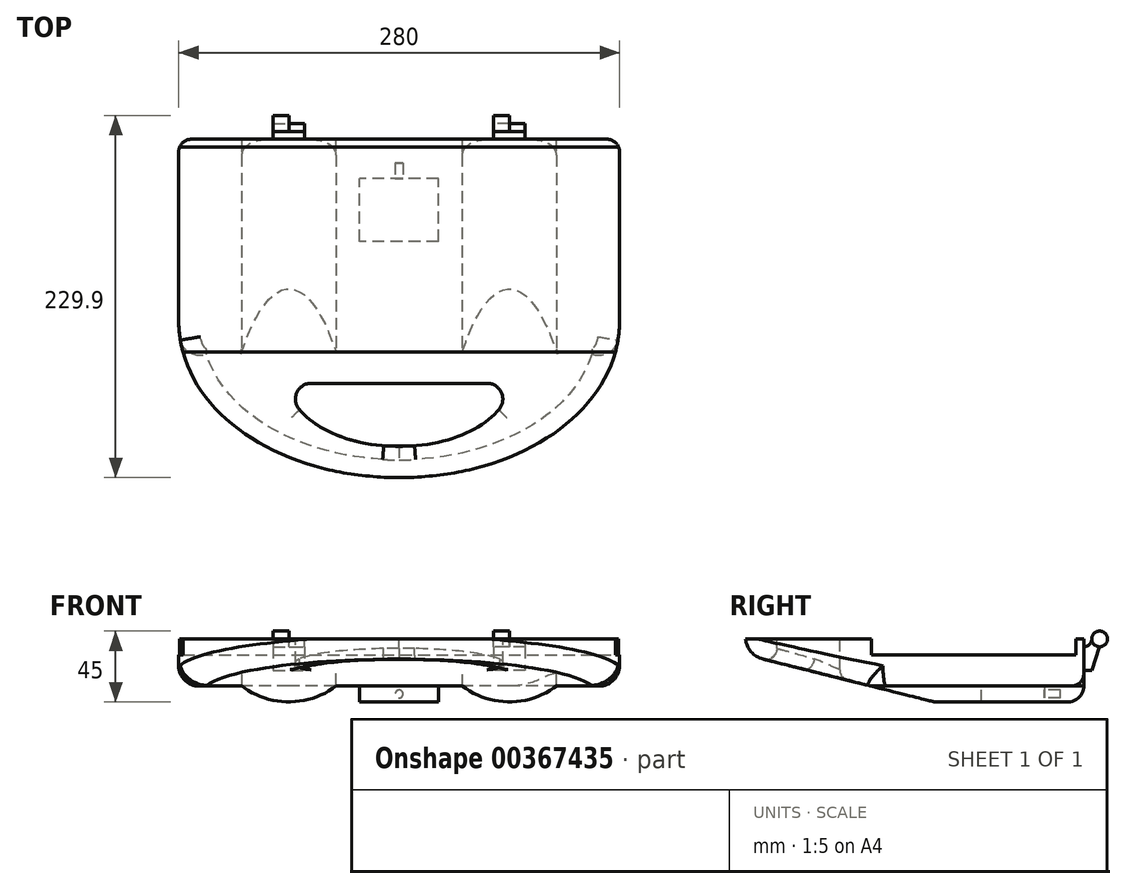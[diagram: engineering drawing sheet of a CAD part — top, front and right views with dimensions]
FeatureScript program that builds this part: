
annotation { "Feature Type Name" : "Feature", "Feature Type Description" : "" }
export const myFeature = defineFeature(function(context is Context, id is Id, definition is map)
    precondition{}
    {
        {
            var Q0;
            Q0=qCreatedBy(makeId("Front.planeOp"),FACE);
            var sketch = newSketch(context, id + "F0", { "sketchPlane" : qUnion([Q0])});
            skLineSegment(sketch, "E0", {"start": v(0, 0) * mm, "end": v(-140, 0) * mm});
            skLineSegment(sketch, "E1", {"start": v(-140, 0) * mm, "end": v(-140, -40) * mm});
            skLineSegment(sketch, "E2", {"start": v(-140, -40) * mm, "end": v(0, -40) * mm});
            skLineSegment(sketch, "E3.MirrorCS", {"start": v(140, -40) * mm, "end": v(0, -40) * mm});
            skLineSegment(sketch, "E4.MirrorCS", {"start": v(0, 0) * mm, "end": v(140, 0) * mm});
            skLineSegment(sketch, "E5.MirrorCS", {"start": v(140, 0) * mm, "end": v(140, -40) * mm});
            skSolve(sketch);
        }
        {
            var Q0;
            Q0=makeQuery(id+"F0.imprint","IMPRINT",FACE,{"disambiguationData":[TD([[makeQuery(id+"F0.imprint","IMPRINT",EDGE,{"derivedFrom":sQuery(id+"F0.wireOp",EDGE,"E0")}),1.0]])]});
            extrude(context, id + "F1", {"entities" : qUnion([Q0]), "endBound" : BoundingType.SYMMETRIC, "depth" : 240 * mm});
        }
        {
            var Q0;
            Q0=makeQuery(id+"F1.opExtrude","SWEPT_FACE",FACE,{"disambiguationData":[OSD([sQuery(id+"F0.wireOp",EDGE,"E5.MirrorCS")])]});
            var sketch = newSketch(context, id + "F2", { "sketchPlane" : qUnion([Q0])});
            skLineSegment(sketch, "E6", {"start": v(-120, 0) * mm, "end": v(-120, -10) * mm});
            skLineSegment(sketch, "E7", {"start": v(-120, -10) * mm, "end": v(-40, -30) * mm});
            skLineSegment(sketch, "E8", {"start": v(-40, -30) * mm, "end": v(0, -40) * mm});
            skLineSegment(sketch, "E9", {"start": v(0, -40) * mm, "end": v(0, -60.45) * mm});
            skLineSegment(sketch, "E10", {"start": v(0, -60.45) * mm, "end": v(-153.05, -60.45) * mm});
            skLineSegment(sketch, "E11", {"start": v(-153.05, -60.45) * mm, "end": v(-153.05, 0) * mm});
            skLineSegment(sketch, "E12", {"start": v(-153.05, 0) * mm, "end": v(-120, 0) * mm});
            skSolve(sketch);
        }
        {
            var Q0;
            Q0=makeQuery(id+"F1.opExtrude","SWEPT_FACE",FACE,{"disambiguationData":[OSD([sQuery(id+"F0.wireOp",EDGE,"E0"),sQuery(id+"F0.wireOp",EDGE,"E4.MirrorCS")])]});
            var sketch = newSketch(context, id + "F3", { "sketchPlane" : qUnion([Q0])});
            skFitSpline(sketch, "E13", {"points": [v(0, -120) * mm, v(-140, -20) * mm], "startDerivative": vector(-228.5, 0) * mm, "endDerivative": vector(0, 173.14) * mm});
            skFitSpline(sketch, "E14.MirrorCS", {"points": [v(0, -120) * mm, v(140, -20) * mm], "startDerivative": vector(228.5, 0) * mm, "endDerivative": vector(0, 173.14) * mm});
            skLineSegment(sketch, "E15", {"start": v(-140, -20) * mm, "end": v(-187.85, -20) * mm});
            skLineSegment(sketch, "E16", {"start": v(-187.85, -20) * mm, "end": v(-187.85, -152.6) * mm});
            skLineSegment(sketch, "E17", {"start": v(-187.85, -152.6) * mm, "end": v(0, -152.6) * mm});
            skLineSegment(sketch, "E18.MirrorCS", {"start": v(187.85, -152.6) * mm, "end": v(0, -152.6) * mm});
            skLineSegment(sketch, "E19.MirrorCS", {"start": v(140, -20) * mm, "end": v(187.85, -20) * mm});
            skLineSegment(sketch, "E20.MirrorCS", {"start": v(187.85, -20) * mm, "end": v(187.85, -152.6) * mm});
            skSolve(sketch);
        }
        {
            var Q0;
            Q0=makeQuery(id+"F1.opExtrude","CAP_FACE",FACE,{"disambiguationData":[OSD([sQuery(id+"F0.wireOp",EDGE,"E0"),sQuery(id+"F0.wireOp",EDGE,"E1"),sQuery(id+"F0.wireOp",EDGE,"E2"),sQuery(id+"F0.wireOp",EDGE,"E3.MirrorCS"),sQuery(id+"F0.wireOp",EDGE,"E4.MirrorCS"),sQuery(id+"F0.wireOp",EDGE,"E5.MirrorCS")])],"isStart":false});
            var sketch = newSketch(context, id + "F4", { "sketchPlane" : qUnion([Q0])});
            skLineSegment(sketch, "E21", {"start": v(-140, -30) * mm, "end": v(-100, -30) * mm});
            skArc(sketch, "E22", {"start": v(-100, -30) * mm, "mid": v(-70, -40) * mm, "end": v(-40, -30) * mm});
            skLineSegment(sketch, "E23", {"start": v(-140, -30) * mm, "end": v(-177.9, -30) * mm});
            skLineSegment(sketch, "E24", {"start": v(-177.9, -30) * mm, "end": v(-177.9, -89.34) * mm});
            skLineSegment(sketch, "E25", {"start": v(-177.9, -89.34) * mm, "end": v(0, -89.34) * mm});
            skPoint(sketch, "E26.endSnap0", {"position": v(0, -40) * mm});
            skLineSegment(sketch, "E27", {"start": v(0, -30) * mm, "end": v(-40, -30) * mm});
            skLineSegment(sketch, "E28.MirrorCS", {"start": v(140, -30) * mm, "end": v(100, -30) * mm});
            skArc(sketch, "E29.MirrorCS", {"start": v(100, -30) * mm, "mid": v(70, -40) * mm, "end": v(40, -30) * mm});
            skLineSegment(sketch, "E30.MirrorCS", {"start": v(140, -30) * mm, "end": v(177.9, -30) * mm});
            skLineSegment(sketch, "E31.MirrorCS", {"start": v(177.9, -30) * mm, "end": v(177.9, -89.34) * mm});
            skLineSegment(sketch, "E32.MirrorCS", {"start": v(177.9, -89.34) * mm, "end": v(0, -89.34) * mm});
            skLineSegment(sketch, "E33.MirrorCS", {"start": v(0, -30) * mm, "end": v(40, -30) * mm});
            skSolve(sketch);
        }
        {
            var Q0;
            {var subQ4=sQuery(id+"F3.wireOp",EDGE,"E13");Q0=makeQuery(id+"F3.imprint","IMPRINT",FACE,{"disambiguationData":[TD([[makeQuery(id+"F3.imprint","IMPRINT",EDGE,{"derivedFrom":subQ4}),-1.0]])]});}
            var sketch = newSketch(context, id + "F5", { "sketchPlane" : qUnion([Q0])});
            skFitSpline(sketch, "E34", {"points": [v(0, -100) * mm, v(-70, -60) * mm], "startDerivative": vector(-116.82, -1.18) * mm, "endDerivative": vector(-0.75, 63.41) * mm});
            skLineSegment(sketch, "E35", {"start": v(-55.84, -60) * mm, "end": v(0, -60) * mm});
            skLineSegment(sketch, "E36.MirrorCS", {"start": v(55.84, -60) * mm, "end": v(0, -60) * mm});
            skFitSpline(sketch, "E37.MirrorCS", {"points": [v(0, -100) * mm, v(70, -60) * mm], "startDerivative": vector(116.82, -1.18) * mm, "endDerivative": vector(0.75, 63.41) * mm});
            skArc(sketch, "E38.filletArc", {"start": v(-55.84, -60) * mm, "mid": v(-64.84, -65.66) * mm, "end": v(-63.66, -76.23) * mm});
            skArc(sketch, "E39.filletArc", {"start": v(63.66, -76.23) * mm, "mid": v(64.84, -65.66) * mm, "end": v(55.84, -60) * mm});
            skSolve(sketch);
        }
        {
            var Q0;
            Q0=qSketchRegion(id+"F3",true);
            extrude(context, id + "F6", {"entities" : qUnion([Q0]), "operationType" : NewBodyOperationType.REMOVE, "oppositeDirection" : true, "depth" : 100 * mm});
        }
        {
            var Q0;
            Q0=qSketchRegion(id+"F4",true);
            extrude(context, id + "F7", {"entities" : qUnion([Q0]), "operationType" : NewBodyOperationType.REMOVE, "oppositeDirection" : true, "depth" : 400 * mm});
        }
        {
            var Q0;
            Q0=qSketchRegion(id+"F2",true);
            extrude(context, id + "F8", {"entities" : qUnion([Q0]), "operationType" : NewBodyOperationType.REMOVE, "oppositeDirection" : true, "depth" : 300 * mm});
        }
        {
            var Q0;
            Q0=qSketchRegion(id+"F5",true);
            extrude(context, id + "F9", {"entities" : qUnion([Q0]), "operationType" : NewBodyOperationType.REMOVE, "oppositeDirection" : true, "depth" : 25 * mm});
        }
        {
            var Q0;
            Q0=makeQuery(id+"F1.opExtrude","SWEPT_FACE",FACE,{"disambiguationData":[OSD([sQuery(id+"F0.wireOp",EDGE,"E5.MirrorCS")])]});
            var sketch = newSketch(context, id + "F10", { "sketchPlane" : qUnion([Q0])});
            skLineSegment(sketch, "E40", {"start": v(-40, 0) * mm, "end": v(-40, -10) * mm});
            skLineSegment(sketch, "E41", {"start": v(-40, -10) * mm, "end": v(90, -10) * mm});
            skLineSegment(sketch, "E42", {"start": v(90, -10) * mm, "end": v(90, 19.27) * mm});
            skLineSegment(sketch, "E43", {"start": v(90, 19.27) * mm, "end": v(-40, 19.27) * mm});
            skLineSegment(sketch, "E44", {"start": v(-40, 19.27) * mm, "end": v(-40, 0) * mm});
            skSolve(sketch);
        }
        {
            var Q0;
            Q0=qSketchRegion(id+"F10",true);
            extrude(context, id + "F11", {"entities" : qUnion([Q0]), "operationType" : NewBodyOperationType.REMOVE, "oppositeDirection" : true, "depth" : 300 * mm});
        }
        {
            var Q0;
            Q0=makeQuery(id+"F1.opExtrude","SWEPT_FACE",FACE,{"disambiguationData":[OSD([sQuery(id+"F0.wireOp",EDGE,"E5.MirrorCS")])]});
            var sketch = newSketch(context, id + "F12", { "sketchPlane" : qUnion([Q0])});
            skLineSegment(sketch, "E45", {"start": v(95, 0) * mm, "end": v(95, -52.5) * mm});
            skLineSegment(sketch, "E46", {"start": v(95, -52.5) * mm, "end": v(129.76, -52.5) * mm});
            skLineSegment(sketch, "E47", {"start": v(129.76, -52.5) * mm, "end": v(129.76, 18.92) * mm});
            skLineSegment(sketch, "E48", {"start": v(129.76, 18.92) * mm, "end": v(95, 18.92) * mm});
            skLineSegment(sketch, "E49", {"start": v(95, 18.92) * mm, "end": v(95, 0) * mm});
            skSolve(sketch);
        }
        {
            var Q0;
            Q0=qSketchRegion(id+"F12",true);
            extrude(context, id + "F13", {"entities" : qUnion([Q0]), "operationType" : NewBodyOperationType.REMOVE, "oppositeDirection" : true, "depth" : 300 * mm});
        }
        {
            var Q0;
            Q0=makeQuery(id+"F13.boolean.opBoolean","COPY",FACE,{"derivedFrom":makeQuery(id+"F13.opExtrude","SWEPT_FACE",FACE,{"disambiguationData":[OSD([sQuery(id+"F12.wireOp",EDGE,"E45"),sQuery(id+"F12.wireOp",EDGE,"E49")])]})});
            var sketch = newSketch(context, id + "F14", { "sketchPlane" : qUnion([Q0])});
            skLineSegment(sketch, "E50", {"start": v(-70, -40) * mm, "end": v(-70, 0) * mm});
            skLineSegment(sketch, "E51", {"start": v(-70, -20) * mm, "end": v(-140, -20) * mm});
            skLineSegment(sketch, "E52", {"start": v(70, -40) * mm, "end": v(70, 0) * mm});
            skLineSegment(sketch, "E53", {"start": v(70, -20) * mm, "end": v(140, -20) * mm});
            skSolve(sketch);
        }
        {
            var Q0;
            Q0=sQuery(id+"F14.wireOp",EDGE,"E51");
            var Q1;
            Q1=sQuery(id+"F14.wireOp",VERTEX,"E51.start");
            cPlane(context, id + "F15", {"entities" : qUnion([Q0, Q1]), "cplaneType" : CPlaneType.LINE_POINT, "offset" : 25 * mm, "width" : 150 * mm, "height" : 150 * mm});
        }
        {
            var Q0;
            Q0=qCreatedBy(id+"F15.planeOp",FACE);
            var sketch = newSketch(context, id + "F16", { "sketchPlane" : qUnion([Q0])});
            skLineSegment(sketch, "E54", {"start": v(95, -5) * mm, "end": v(95, -20) * mm});
            skLineSegment(sketch, "E55", {"start": v(95, -20) * mm, "end": v(100, -20) * mm});
            skLineSegment(sketch, "E56", {"start": v(95, -5) * mm, "end": v(95, -5) * mm});
            skLineSegment(sketch, "E57", {"start": v(95, -20) * mm, "end": v(0, -20) * mm});
            skLineSegment(sketch, "E58", {"start": v(0, -20) * mm, "end": v(0, 0) * mm});
            skLineSegment(sketch, "E59", {"start": v(105, -5) * mm, "end": v(100, -20) * mm});
            skLineSegment(sketch, "E60", {"start": v(105, -5) * mm, "end": v(105, 0) * mm});
            skCircle(sketch, "E61", {"center": v(105, 0) * mm, "radius": 5 * mm});
            skLineSegment(sketch, "E62", {"start": v(100, 0) * mm, "end": v(100, 0) * mm});
            skPoint(sketch, "E63.newPointA", {"position": v(100, -5) * mm});
            skPoint(sketch, "E63.newPointB", {"position": v(105, -5) * mm});
            skArc(sketch, "E63.filletArc", {"start": v(95, -5) * mm, "mid": v(98.54, -3.54) * mm, "end": v(100, 0) * mm});
            skSolve(sketch);
        }
        {
            var Q0;
            Q0=sQuery(id+"F14.wireOp",EDGE,"E53");
            var Q1;
            Q1=sQuery(id+"F14.wireOp",VERTEX,"E53.start");
            cPlane(context, id + "F17", {"entities" : qUnion([Q0, Q1]), "cplaneType" : CPlaneType.LINE_POINT, "offset" : 25 * mm, "width" : 150 * mm, "height" : 150 * mm});
        }
        {
            var Q0;
            Q0=qCreatedBy(id+"F17.planeOp",FACE);
            var sketch = newSketch(context, id + "F18", { "sketchPlane" : qUnion([Q0])});
            skLineSegment(sketch, "E64", {"start": v(-95, -5) * mm, "end": v(-95, -20) * mm});
            skLineSegment(sketch, "E65", {"start": v(-95, -20) * mm, "end": v(-100, -20) * mm});
            skLineSegment(sketch, "E66", {"start": v(-100, -20) * mm, "end": v(-105, -5) * mm});
            skLineSegment(sketch, "E67", {"start": v(-95, -5) * mm, "end": v(-95, -5) * mm});
            skPoint(sketch, "E68.newPointA", {"position": v(-100, -5) * mm});
            skPoint(sketch, "E68.newPointB", {"position": v(-105, -5) * mm});
            skLineSegment(sketch, "E69", {"start": v(-95, -20) * mm, "end": v(0, -20) * mm});
            skLineSegment(sketch, "E70", {"start": v(0, -20) * mm, "end": v(0, 0) * mm});
            skLineSegment(sketch, "E71", {"start": v(-105, -5) * mm, "end": v(-105, 0) * mm});
            skCircle(sketch, "E72", {"center": v(-105, 0) * mm, "radius": 5 * mm});
            skLineSegment(sketch, "E73", {"start": v(-100, 0) * mm, "end": v(-100, 0) * mm});
            skArc(sketch, "E74.filletArc", {"start": v(-100, 0) * mm, "mid": v(-98.54, -3.54) * mm, "end": v(-95, -5) * mm});
            skSolve(sketch);
        }
        {
            var Q0;
            Q0=makeQuery(id+"F8.boolean.opBoolean","INTERSECT",EDGE,{"derivedFrom":[makeQuery(id+"F6.boolean.opBoolean","COPY",FACE,{"derivedFrom":makeQuery(id+"F6.opExtrude","SWEPT_FACE",FACE,{"disambiguationData":[OSD([sQuery(id+"F3.wireOp",EDGE,"E14.MirrorCS")])]})}),makeQuery(id+"F8.opExtrude","SWEPT_FACE",FACE,{"disambiguationData":[OSD([sQuery(id+"F2.wireOp",EDGE,"E7"),sQuery(id+"F2.wireOp",EDGE,"E8")])]})]});
            fillet(context, id + "F19", {"entities" : qUnion([Q0]), "radius" : 15 * mm, "tangentPropagation" : true, "allowEdgeOverflow" : false});
        }
        {
            var Q0;
            Q0=makeQuery(id+"F7.boolean.opBoolean","INTERSECT",EDGE,{"derivedFrom":[makeQuery(id+"F1.opExtrude","SWEPT_FACE",FACE,{"disambiguationData":[OSD([sQuery(id+"F0.wireOp",EDGE,"E5.MirrorCS")])]}),makeQuery(id+"F7.opExtrude","SWEPT_FACE",FACE,{"disambiguationData":[OSD([sQuery(id+"F4.wireOp",EDGE,"E28.MirrorCS"),sQuery(id+"F4.wireOp",EDGE,"E30.MirrorCS")])]})]});
            fillet(context, id + "F20", {"entities" : qUnion([Q0]), "radius" : 13 * mm, "tangentPropagation" : true, "allowEdgeOverflow" : false});
        }
        {
            var Q0;
            Q0=makeQuery(id+"F7.boolean.opBoolean","INTERSECT",EDGE,{"derivedFrom":[makeQuery(id+"F1.opExtrude","SWEPT_FACE",FACE,{"disambiguationData":[OSD([sQuery(id+"F0.wireOp",EDGE,"E1")])]}),makeQuery(id+"F7.opExtrude","SWEPT_FACE",FACE,{"disambiguationData":[OSD([sQuery(id+"F4.wireOp",EDGE,"E21"),sQuery(id+"F4.wireOp",EDGE,"E23")])]})]});
            fillet(context, id + "F21", {"entities" : qUnion([Q0]), "radius" : 13 * mm, "tangentPropagation" : true, "allowEdgeOverflow" : false});
        }
        {
            var Q0;
            Q0=makeQuery(id+"F9.boolean.opBoolean","INTERSECT",EDGE,{"derivedFrom":[makeQuery(id+"F8.boolean.opBoolean","COPY",FACE,{"derivedFrom":makeQuery(id+"F8.opExtrude","SWEPT_FACE",FACE,{"disambiguationData":[OSD([sQuery(id+"F2.wireOp",EDGE,"E7"),sQuery(id+"F2.wireOp",EDGE,"E8")])]})}),makeQuery(id+"F9.opExtrude","SWEPT_FACE",FACE,{"disambiguationData":[OSD([sQuery(id+"F5.wireOp",EDGE,"E34")])]})]});
            fillet(context, id + "F22", {"entities" : qUnion([Q0]), "radius" : 7 * mm, "tangentPropagation" : true, "allowEdgeOverflow" : false});
        }
        {
            var Q0;
            Q0=makeQuery(id+"F13.boolean.opBoolean","INTERSECT",EDGE,{"derivedFrom":[makeQuery(id+"F7.boolean.opBoolean","COPY",FACE,{"derivedFrom":makeQuery(id+"F7.opExtrude","SWEPT_FACE",FACE,{"disambiguationData":[OSD([sQuery(id+"F4.wireOp",EDGE,"E22")])]})}),makeQuery(id+"F13.opExtrude","SWEPT_FACE",FACE,{"disambiguationData":[OSD([sQuery(id+"F12.wireOp",EDGE,"E45"),sQuery(id+"F12.wireOp",EDGE,"E49")])]})]});
            fillet(context, id + "F23", {"entities" : qUnion([Q0]), "radius" : 10 * mm, "tangentPropagation" : true, "allowEdgeOverflow" : false});
        }
        {
            var Q0;
            Q0=makeQuery(id+"F13.boolean.opBoolean","INTERSECT",EDGE,{"derivedFrom":[makeQuery(id+"F7.boolean.opBoolean","COPY",FACE,{"derivedFrom":makeQuery(id+"F7.opExtrude","SWEPT_FACE",FACE,{"disambiguationData":[OSD([sQuery(id+"F4.wireOp",EDGE,"E29.MirrorCS")])]})}),makeQuery(id+"F13.opExtrude","SWEPT_FACE",FACE,{"disambiguationData":[OSD([sQuery(id+"F12.wireOp",EDGE,"E45"),sQuery(id+"F12.wireOp",EDGE,"E49")])]})]});
            fillet(context, id + "F24", {"entities" : qUnion([Q0]), "radius" : 10 * mm, "tangentPropagation" : true, "allowEdgeOverflow" : false});
        }
        {
            var Q0;
            Q0=makeQuery(id+"F13.boolean.opBoolean","INTERSECT",EDGE,{"derivedFrom":[makeQuery(id+"F7.boolean.opBoolean","COPY",FACE,{"derivedFrom":makeQuery(id+"F7.opExtrude","SWEPT_FACE",FACE,{"disambiguationData":[OSD([sQuery(id+"F4.wireOp",EDGE,"E27"),sQuery(id+"F4.wireOp",EDGE,"E33.MirrorCS")])]})}),makeQuery(id+"F13.opExtrude","SWEPT_FACE",FACE,{"disambiguationData":[OSD([sQuery(id+"F12.wireOp",EDGE,"E45"),sQuery(id+"F12.wireOp",EDGE,"E49")])]})]});
            fillet(context, id + "F25", {"entities" : qUnion([Q0]), "radius" : 8 * mm, "tangentPropagation" : true, "allowEdgeOverflow" : false});
        }
        {
            var Q0;
            Q0=makeQuery(id+"F18.imprint","IMPRINT",FACE,{"disambiguationData":[TD([[makeQuery(id+"F18.imprint","IMPRINT",EDGE,{"derivedFrom":sQuery(id+"F18.wireOp",EDGE,"E64")}),-1.0]])]});
            extrude(context, id + "F26", {"entities" : qUnion([Q0]), "operationType" : NewBodyOperationType.ADD, "endBound" : BoundingType.SYMMETRIC, "depth" : 20 * mm});
        }
        {
            var Q0;
            {var subQ0=sQuery(id+"F18.wireOp",EDGE,"E72");var subQ1=makeQuery(id+"F18.imprint","INTERSECT",VERTEX,{"derivedFrom":[sQuery(id+"F18.wireOp",EDGE,"E66"),subQ0]});Q0=makeQuery(id+"F18.imprint","IMPRINT",FACE,{"disambiguationData":[TD([[makeQuery(id+"F18.imprint","IMPRINT",EDGE,{"disambiguationData":[TD([[subQ1,1.0]])],"derivedFrom":subQ0}),1.0]])]});}
            extrude(context, id + "F27", {"entities" : qUnion([Q0]), "operationType" : NewBodyOperationType.ADD, "depth" : 10 * mm});
        }
        {
            var Q0;
            Q0=makeQuery(id+"F16.imprint","IMPRINT",FACE,{"disambiguationData":[TD([[makeQuery(id+"F16.imprint","IMPRINT",EDGE,{"derivedFrom":sQuery(id+"F16.wireOp",EDGE,"E54")}),1.0]])]});
            extrude(context, id + "F28", {"entities" : qUnion([Q0]), "operationType" : NewBodyOperationType.ADD, "endBound" : BoundingType.SYMMETRIC, "depth" : 20 * mm});
        }
        {
            var Q0;
            {var subQ0=sQuery(id+"F16.wireOp",EDGE,"E61");var subQ1=makeQuery(id+"F16.imprint","INTERSECT",VERTEX,{"derivedFrom":[sQuery(id+"F16.wireOp",EDGE,"E59"),subQ0]});Q0=makeQuery(id+"F16.imprint","IMPRINT",FACE,{"disambiguationData":[TD([[makeQuery(id+"F16.imprint","IMPRINT",EDGE,{"disambiguationData":[TD([[subQ1,1.0]])],"derivedFrom":subQ0}),1.0]])]});}
            extrude(context, id + "F29", {"entities" : qUnion([Q0]), "operationType" : NewBodyOperationType.ADD, "oppositeDirection" : true, "depth" : 10 * mm});
        }
        {
            var Q0;
            Q0=qCreatedBy(makeId("Right.planeOp"),FACE);
            var sketch = newSketch(context, id + "F30", { "sketchPlane" : qUnion([Q0])});
            skLineSegment(sketch, "E75", {"start": v(0, 0) * mm, "end": v(60, 0) * mm});
            skLineSegment(sketch, "E76", {"start": v(60, 0) * mm, "end": v(60, -30) * mm});
            skLineSegment(sketch, "E77", {"start": v(60, -30) * mm, "end": v(70, -30) * mm});
            skLineSegment(sketch, "E78", {"start": v(70, -30) * mm, "end": v(70, -40) * mm});
            skLineSegment(sketch, "E79", {"start": v(70, -40) * mm, "end": v(30, -40) * mm});
            skLineSegment(sketch, "E80", {"start": v(30, -40) * mm, "end": v(30, -30) * mm});
            skLineSegment(sketch, "E81", {"start": v(30, -30) * mm, "end": v(60, -30) * mm});
            skSolve(sketch);
        }
        {
            var Q0;
            Q0=makeQuery(id+"F30.imprint","IMPRINT",FACE,{"disambiguationData":[TD([[makeQuery(id+"F30.imprint","IMPRINT",EDGE,{"derivedFrom":sQuery(id+"F30.wireOp",EDGE,"E77")}),-1.0]])]});
            extrude(context, id + "F31", {"entities" : qUnion([Q0]), "operationType" : NewBodyOperationType.ADD, "endBound" : BoundingType.SYMMETRIC, "depth" : 50 * mm});
        }
        {
            var Q0;
            Q0=qCreatedBy(makeId("Right.planeOp"),FACE);
            var sketch = newSketch(context, id + "F32", { "sketchPlane" : qUnion([Q0])});
            skLineSegment(sketch, "E82", {"start": v(0, 0) * mm, "end": v(70, 0) * mm});
            skLineSegment(sketch, "E83", {"start": v(70, 0) * mm, "end": v(70, -35) * mm});
            skLineSegment(sketch, "E84", {"start": v(70, -35) * mm, "end": v(80, -35) * mm});
            skLineSegment(sketch, "E85", {"start": v(80, -35) * mm, "end": v(80, -32.5) * mm});
            skLineSegment(sketch, "E86", {"start": v(80, -32.5) * mm, "end": v(70, -32.5) * mm});
            skLineSegment(sketch, "E87", {"start": v(70, -32.5) * mm, "end": v(70, -35) * mm});
            skSolve(sketch);
        }
        {
            var Q0;
            Q0=makeQuery(id+"F32.imprint","IMPRINT",FACE,{"disambiguationData":[TD([[makeQuery(id+"F32.imprint","IMPRINT",EDGE,{"derivedFrom":sQuery(id+"F32.wireOp",EDGE,"E84")}),1.0]])]});
            var Q1;
            Q1=sQuery(id+"F32.wireOp",EDGE,"E84");
            revolve(context, id + "F33", {"operationType" : NewBodyOperationType.ADD, "entities" : qUnion([Q0]), "axis" : qUnion([Q1]), "revolveType" : RevolveType.FULL});
        }
    });
